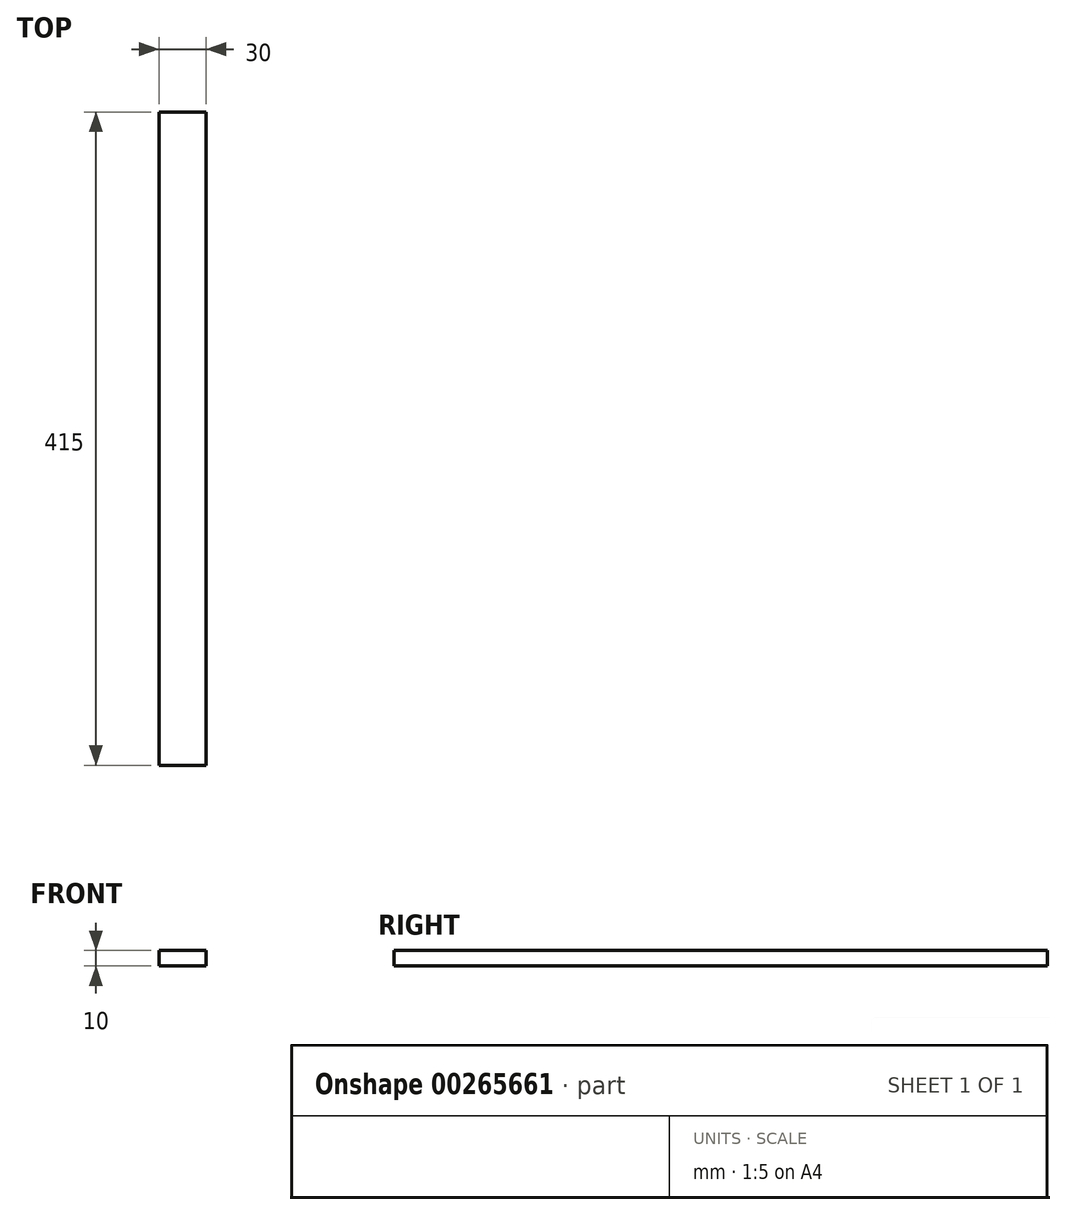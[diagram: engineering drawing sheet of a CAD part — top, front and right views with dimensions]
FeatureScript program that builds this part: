
annotation { "Feature Type Name" : "Feature", "Feature Type Description" : "" }
export const myFeature = defineFeature(function(context is Context, id is Id, definition is map)
    precondition{}
    {
        {
            var Q0;
            Q0=qCreatedBy(makeId("Front.planeOp"),FACE);
            var sketch = newSketch(context, id + "F0", { "sketchPlane" : qUnion([Q0])});
            skLineSegment(sketch, "E0.bottom", {"start": v(0, 0) * mm, "end": v(30, 0) * mm});
            skLineSegment(sketch, "E0.top", {"start": v(0, -10) * mm, "end": v(30, -10) * mm});
            skLineSegment(sketch, "E0.left", {"start": v(0, 0) * mm, "end": v(0, -10) * mm});
            skLineSegment(sketch, "E0.right", {"start": v(30, 0) * mm, "end": v(30, -10) * mm});
            skSolve(sketch);
        }
        {
            var Q0;
            Q0=qSketchRegion(id+"F0",true);
            extrude(context, id + "F1", {"entities" : qUnion([Q0]), "depth" : 415 * mm});
        }
    });
